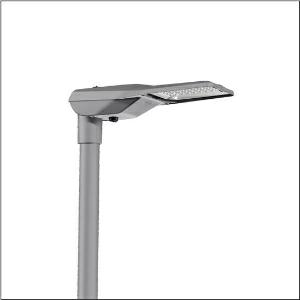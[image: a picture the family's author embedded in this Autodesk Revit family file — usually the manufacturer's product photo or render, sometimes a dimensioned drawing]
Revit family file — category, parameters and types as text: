
# Revit family: streetlight_sl_21_iq_mini___st1_0a_5xe2d51y08jb_5dfa
name_source: partatom
category: Lighting Fixtures
units: mm (PartAtom-declared; Revit-internal decimal feet)

## family parameters
Cut with Voids When Loaded = No
Host = Face
Light Source = No
Part Type = Normal
Room Calculation Point = No
Round Connector Dimension = Use Diameter
Shared = No

## types (1)
- --- (1 x LED, 9850 lm, 72.5 W, 3000K)
    Apparent Load = 73 VA
    CIE Flux Codes = 40 73 97 100 100
    Color Rendering = 80
    Color Temperature = 3000K
    Default Elevation = 1800 mm
    Description = Streetlight SL 21 iQ mini, mast luminaire, primary light control with lens, of PMMA, primary optical cover: cover, of toughened safety glass, transparent, light distribution: ST1.0a, light emission: direct distribution, primary light characteristic: asymmetric, installation type: post-top, side-entry, LED, High Power LED, rated luminous flux: 9.850lm, luminous efficacy: 136lm/W, light colour: 830, colour temperature: 3000K, control: pre-setting: logarithmic dimming characteristic, Street-Remote, Auto-Match, Temp-Guard, Lumen-Switch, Night-Set, Smart-Wire, Light-Fading, Desk-Remote (wireless, voltage-free reading and setting of iQ features in the workshop via application-optimized NFC function/RFID function), optimised constant luminous flux control (CLO 2.0), mains connection: 220..240V, AC, 50/60Hz, start of lifetime: 73W, end of service life: 76W, reduction: 33W, luminaire housing, of diecast aluminium, powder-coated, Siteco® metallic grey (DB 702S), corrosivity category C5 mid according to DIN EN ISO 12944, please order mast flange separately, inclination adjustable: 0°, 5°, 10°, 15°, sealing non-destructively replaceable, multi-level sealing system, length: 628mm, width: 235mm, height: 110mm, mast flange for spigot size: 42mm (side-entry): 5XC10008XM4, 60/48mm (side-entry/post-top): 5XC10108XM2, 76/60mm (side-entry/post-top): 5XC10108XM1, Smart Interface below and above, protection rating (complete): IP66, insulation class (complete): insulation class II (safety insulation), certification: CE, ENEC, ENEC+, VDE, impact resistance: IK09, permissible operating ambient temperature for outdoor applications: -40..+50°C, standard-compliant lighting for roads and squares, packaging unit: 1 piece

Light Distribution: ST1.0a
    Height = 110 mm
    Lamp = 1 x LED
    Lamp Light Flux = 9850 lm
    Lamp Power = 72.5 W
    Lamp count = 1
    Length = 625 mm
    Luminous efficacy = 136 lm/W
    Manufacturer = Siteco
    ModVariant = No
    Model = 5XE2D51Y08JB
    Number of Poles = 1
    OnlyDefault = Yes
    Power Factor = 1
    Product Name = Streetlight SL 21 iQ mini | ST1.0a
    Product group = mast luminaire | pylon top
    ProductGroupID = 6100
    Protection Class = Protection class II
    Protection Degree = IP 66
    RLX_Detail_Level = 1
    RLX_Emergency_Light_Flux = 0 lm
    RLX_Emergency_Type = 0
    RLX_Emergency_Type_DB = No
    RlxData = <blob elided: 92841 chars, md5=e217ac48>
    Socket = socket
    Standby Power = 0 W
    System Light Flux = 9850 lm
    System Power = 73 W
    Type Comments = factory setting: luminous flux: 100 % | dim-lin: 254 | 755 mA
    Type Image = l_1003514.jpg
    URL = http://relux.com
    VarID = @adj_082881
    Voltage = 0 V
    Weight = 0.00 kg
    Width = 234 mm

## geometry (parser evidence)
native form markers: Blend x4, Sweep x9
no freeform markers — native parametric forms only
